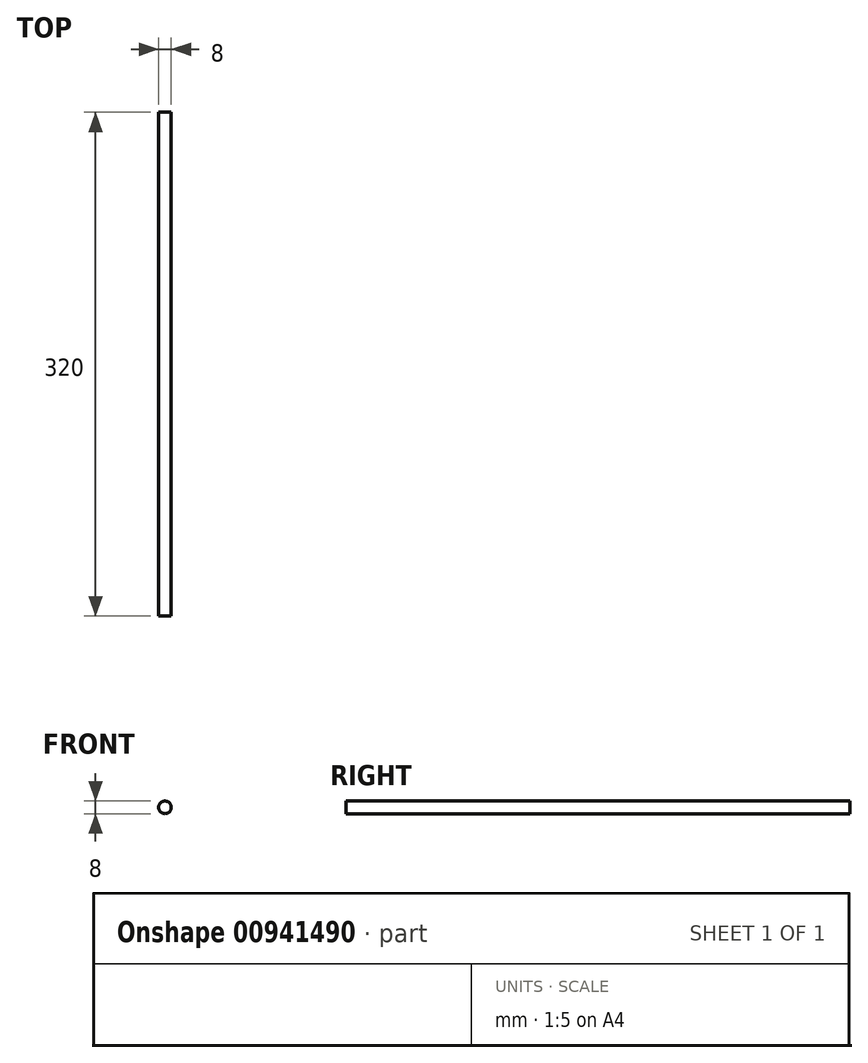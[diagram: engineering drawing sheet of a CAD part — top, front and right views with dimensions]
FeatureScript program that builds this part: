
annotation { "Feature Type Name" : "Feature", "Feature Type Description" : "" }
export const myFeature = defineFeature(function(context is Context, id is Id, definition is map)
    precondition{}
    {
        {
            var Q0;
            Q0=qCreatedBy(makeId("Front.planeOp"),FACE);
            var sketch = newSketch(context, id + "F0", { "sketchPlane" : qUnion([Q0])});
            skCircle(sketch, "E0", {"center": v(0, 0) * mm, "radius": 4 * mm});
            skSolve(sketch);
        }
        {
            var Q0;
            Q0=makeQuery(id+"F0.imprint","IMPRINT",FACE,{"disambiguationData":[TD([[makeQuery(id+"F0.imprint","IMPRINT",EDGE,{"derivedFrom":sQuery(id+"F0.wireOp",EDGE,"E0")}),1.0]])]});
            extrude(context, id + "F1", {"entities" : qUnion([Q0]), "depth" : 320 * mm, "offsetDistance" : 25 * mm});
        }
    });
